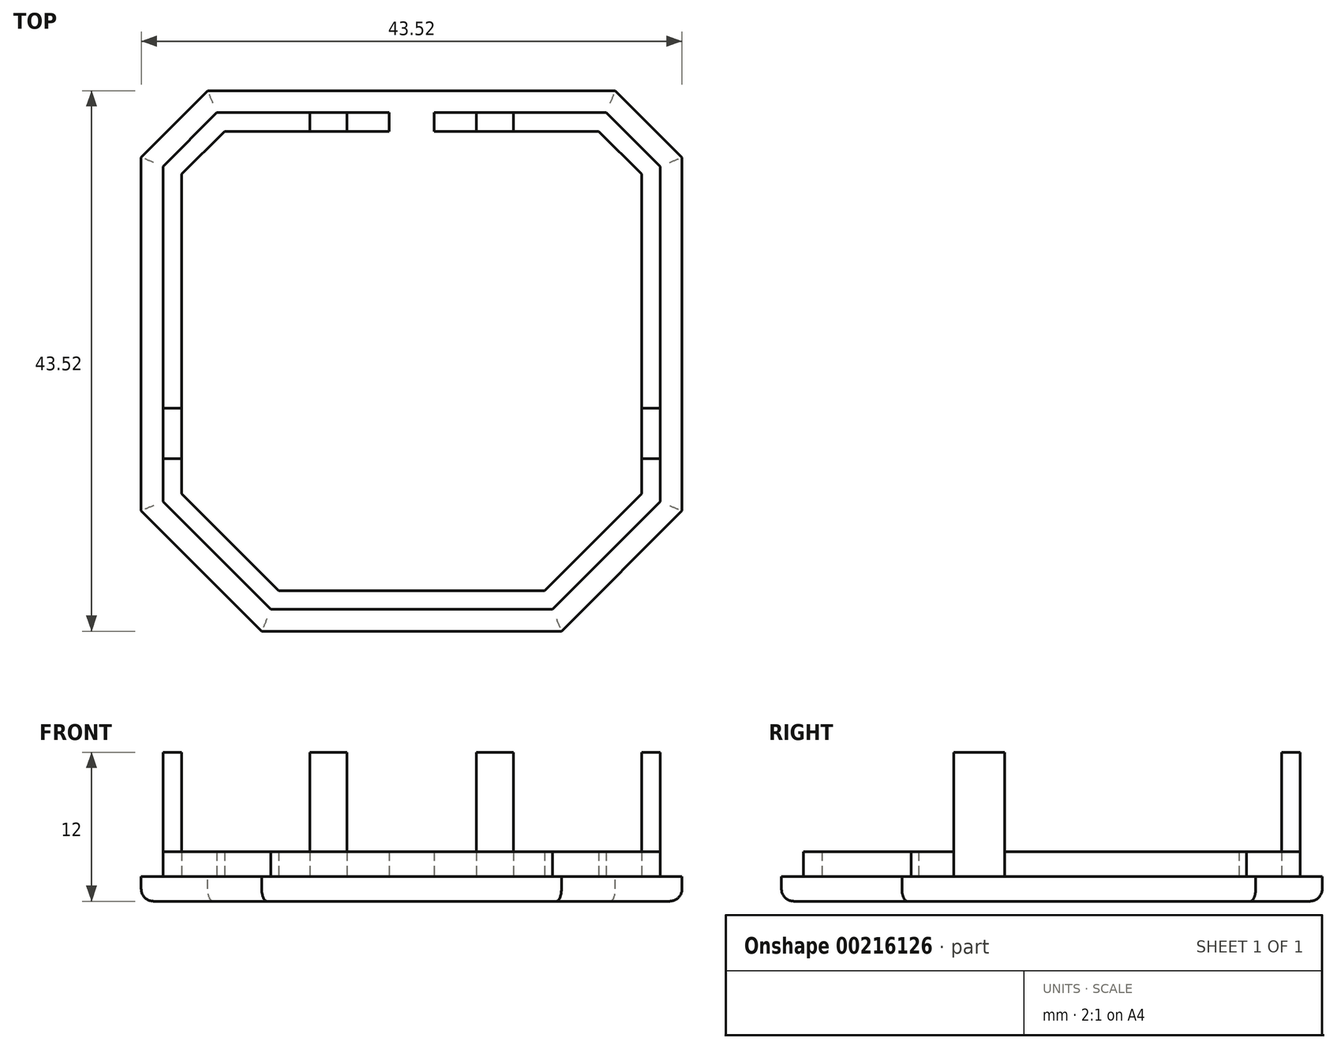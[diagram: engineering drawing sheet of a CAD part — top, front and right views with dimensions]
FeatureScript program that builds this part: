
annotation { "Feature Type Name" : "Feature", "Feature Type Description" : "" }
export const myFeature = defineFeature(function(context is Context, id is Id, definition is map)
    precondition{}
    {
        {
            var Q0;
            Q0=qCreatedBy(makeId("Top.planeOp"),FACE);
            var sketch = newSketch(context, id + "F0", { "sketchPlane" : qUnion([Q0])});
            skLineSegment(sketch, "E0", {"start": v(-56.85, 1.5) * mm, "end": v(-30.15, 1.5) * mm, "construction": true});
            skLineSegment(sketch, "E1", {"start": v(-0.95, 49.22) * mm, "end": v(-0.95, -52.62) * mm, "construction": true});
            skPoint(sketch, "E2", {"position": v(28.25, 1.5) * mm});
            skLineSegment(sketch, "E3.trimOffspring", {"start": v(-27.15, 1.5) * mm, "end": v(25.25, 1.5) * mm, "construction": true});
            skLineSegment(sketch, "E4.trimOffspring", {"start": v(28.25, 1.5) * mm, "end": v(65.36, 1.5) * mm, "construction": true});
            skLineSegment(sketch, "E5.bottom", {"start": v(10.38, -21.7) * mm, "end": v(-12.28, -21.7) * mm});
            skLineSegment(sketch, "E5.top", {"start": v(14.72, 18.3) * mm, "end": v(-16.62, 18.3) * mm});
            skLineSegment(sketch, "E5.left", {"start": v(19.05, -13.03) * mm, "end": v(19.05, 13.97) * mm});
            skLineSegment(sketch, "E5.right", {"start": v(-20.95, -13.03) * mm, "end": v(-20.95, 13.97) * mm});
            skPoint(sketch, "E5.middle", {"position": v(-0.95, -1.7) * mm});
            skPoint(sketch, "E6.visualSharp", {"position": v(-20.95, 18.3) * mm});
            skPoint(sketch, "E7.visualSharp", {"position": v(19.05, 18.3) * mm});
            skPoint(sketch, "E8.visualSharp", {"position": v(19.05, -21.7) * mm});
            skPoint(sketch, "E9.visualSharp", {"position": v(-20.95, -21.7) * mm});
            skLineSegment(sketch, "E10", {"start": v(-20.95, 13.97) * mm, "end": v(-16.62, 18.3) * mm});
            skLineSegment(sketch, "E11", {"start": v(14.72, 18.3) * mm, "end": v(19.05, 13.97) * mm});
            skLineSegment(sketch, "E12", {"start": v(19.05, -13.03) * mm, "end": v(10.38, -21.7) * mm});
            skLineSegment(sketch, "E13", {"start": v(-20.95, -13.03) * mm, "end": v(-12.28, -21.7) * mm});
            skLineSegment(sketch, "E14.0", {"start": v(-22.71, -13.76) * mm, "end": v(-13.01, -23.46) * mm});
            skLineSegment(sketch, "E14.1", {"start": v(11.1, -23.46) * mm, "end": v(-13.01, -23.46) * mm});
            skLineSegment(sketch, "E14.2", {"start": v(-22.71, -13.76) * mm, "end": v(-22.71, 14.7) * mm});
            skLineSegment(sketch, "E14.3", {"start": v(20.81, -13.76) * mm, "end": v(11.1, -23.46) * mm});
            skLineSegment(sketch, "E14.4", {"start": v(-22.71, 14.7) * mm, "end": v(-17.35, 20.06) * mm});
            skLineSegment(sketch, "E14.5", {"start": v(15.45, 20.06) * mm, "end": v(-17.35, 20.06) * mm});
            skLineSegment(sketch, "E14.6", {"start": v(15.45, 20.06) * mm, "end": v(20.81, 14.7) * mm});
            skLineSegment(sketch, "E14.7", {"start": v(20.81, -13.76) * mm, "end": v(20.81, 14.7) * mm});
            skPoint(sketch, "E15.orphan", {"position": v(32.35, 7.83) * mm});
            skPoint(sketch, "E16.orphan", {"position": v(32.35, -4.83) * mm});
            skPoint(sketch, "E17.orphan", {"position": v(-30.54, -4.83) * mm});
            skPoint(sketch, "E18.orphan", {"position": v(-30.54, 7.83) * mm});
            skPoint(sketch, "E19.center.orphan", {"position": v(-9.84, 17.42) * mm});
            skPoint(sketch, "E20.center.orphan", {"position": v(-9.84, -20.93) * mm});
            skLineSegment(sketch, "E21.0", {"start": v(14.1, 16.8) * mm, "end": v(17.55, 13.35) * mm});
            skLineSegment(sketch, "E21.1", {"start": v(17.55, -12.4) * mm, "end": v(17.55, 13.35) * mm});
            skLineSegment(sketch, "E21.2", {"start": v(14.1, 16.8) * mm, "end": v(-16, 16.8) * mm});
            skLineSegment(sketch, "E21.3", {"start": v(17.55, -12.4) * mm, "end": v(9.76, -20.2) * mm});
            skLineSegment(sketch, "E21.4", {"start": v(-19.45, 13.35) * mm, "end": v(-16, 16.8) * mm});
            skLineSegment(sketch, "E21.5", {"start": v(-19.45, -12.4) * mm, "end": v(-19.45, 13.35) * mm});
            skLineSegment(sketch, "E21.6", {"start": v(-19.45, -12.4) * mm, "end": v(-11.66, -20.2) * mm});
            skLineSegment(sketch, "E21.7", {"start": v(9.76, -20.2) * mm, "end": v(-11.66, -20.2) * mm});
            skLineSegment(sketch, "E22", {"start": v(-20.95, -9.58) * mm, "end": v(-19.45, -9.58) * mm});
            skLineSegment(sketch, "E23", {"start": v(-19.45, -9.58) * mm, "end": v(-19.45, -5.5) * mm});
            skLineSegment(sketch, "E24", {"start": v(-19.45, -5.5) * mm, "end": v(-20.95, -5.5) * mm});
            skLineSegment(sketch, "E25.MirrorCS", {"start": v(19.05, -9.58) * mm, "end": v(17.55, -9.58) * mm});
            skLineSegment(sketch, "E26.MirrorCS", {"start": v(17.55, -5.5) * mm, "end": v(19.05, -5.5) * mm});
            skLineSegment(sketch, "E27", {"start": v(-9.15, 18.3) * mm, "end": v(-9.15, 16.8) * mm});
            skLineSegment(sketch, "E28", {"start": v(-9.15, 16.8) * mm, "end": v(-6.15, 16.8) * mm});
            skLineSegment(sketch, "E29", {"start": v(-6.15, 16.8) * mm, "end": v(-6.15, 18.3) * mm});
            skPoint(sketch, "E30.end.orphan", {"position": v(-2.77, 18.3) * mm});
            skPoint(sketch, "E30.start.orphan", {"position": v(-2.77, 16.8) * mm});
            skPoint(sketch, "E31.MirrorCS.end.orphan", {"position": v(0.86, 18.3) * mm});
            skPoint(sketch, "E31.MirrorCS.start.orphan", {"position": v(0.86, 16.8) * mm});
            skLineSegment(sketch, "E32.MirrorCS", {"start": v(7.25, 18.3) * mm, "end": v(7.25, 16.8) * mm});
            skLineSegment(sketch, "E33.MirrorCS", {"start": v(4.25, 16.8) * mm, "end": v(4.25, 18.3) * mm});
            skLineSegment(sketch, "E34.MirrorCS", {"start": v(7.25, 16.8) * mm, "end": v(4.25, 16.8) * mm});
            skLineSegment(sketch, "E35", {"start": v(-2.77, 18.3) * mm, "end": v(-2.77, 16.8) * mm});
            skLineSegment(sketch, "E36", {"start": v(0.86, 18.3) * mm, "end": v(0.86, 16.8) * mm});
            skSolve(sketch);
        }
        {
            var Q0;
            Q0 = qSketchRegion(id + "F0", true);
            var Q1;
            Q1=makeQuery(id+"F0.imprint","IMPRINT",FACE,{"disambiguationData":[TD([[makeQuery(id+"F0.imprint","IMPRINT",EDGE,{"derivedFrom":sQuery(id+"F0.wireOp",EDGE,"E5.left")}),1.0]])]});
            var Q2;
            {var subQ0=sQuery(id+"F0.wireOp",EDGE,"E19");Q2=makeQuery(id+"F0.imprint","IMPRINT",FACE,{"disambiguationData":[TD([[makeQuery(id+"F0.imprint","IMPRINT",EDGE,{"derivedFrom":subQ0}),1.0]])]});}
            var Q3;
            {var subQ0=sQuery(id+"F0.wireOp",EDGE,"4e1065f4-3c0d-4255-a0ed-20f52c7de798.MirrorC");Q3=makeQuery(id+"F0.imprint","IMPRINT",FACE,{"disambiguationData":[TD([[makeQuery(id+"F0.imprint","IMPRINT",EDGE,{"derivedFrom":subQ0}),-1.0]])]});}
            var Q4;
            {var subQ0=sQuery(id+"F0.wireOp",EDGE,"f484cf5a-7d54-4800-a930-bd30d667224f.MirrorC");Q4=makeQuery(id+"F0.imprint","IMPRINT",FACE,{"disambiguationData":[TD([[makeQuery(id+"F0.imprint","IMPRINT",EDGE,{"derivedFrom":subQ0}),-1.0]])]});}
            var Q5;
            {var subQ0=sQuery(id+"F0.wireOp",EDGE,"E20");Q5=makeQuery(id+"F0.imprint","IMPRINT",FACE,{"disambiguationData":[TD([[makeQuery(id+"F0.imprint","IMPRINT",EDGE,{"derivedFrom":subQ0}),1.0]])]});}
            var Q6;
            Q6=makeQuery(id+"F0.imprint","IMPRINT",FACE,{"disambiguationData":[TD([[makeQuery(id+"F0.imprint","IMPRINT",EDGE,{"derivedFrom":sQuery(id+"F0.wireOp",EDGE,"E21.0")}),-1.0]])]});
            var Q7;
            {var subQ1=sQuery(id+"F0.wireOp",EDGE,"E11");Q7=makeQuery(id+"F0.imprint","IMPRINT",FACE,{"disambiguationData":[TD([[makeQuery(id+"F0.imprint","IMPRINT",EDGE,{"derivedFrom":subQ1}),-1.0]])]});}
            var Q8;
            {var subQ0=sQuery(id+"F0.wireOp",EDGE,"E10");Q8=makeQuery(id+"F0.imprint","IMPRINT",FACE,{"disambiguationData":[TD([[makeQuery(id+"F0.imprint","IMPRINT",EDGE,{"derivedFrom":subQ0}),-1.0]])]});}
            var Q9;
            Q9=makeQuery(id+"F0.imprint","IMPRINT",FACE,{"disambiguationData":[TD([[makeQuery(id+"F0.imprint","IMPRINT",EDGE,{"derivedFrom":sQuery(id+"F0.wireOp",EDGE,"E5.bottom")}),-1.0]])]});
            var Q10;
            {var subQ0=sQuery(id+"F0.wireOp",EDGE,"E30");Q10=makeQuery(id+"F0.imprint","IMPRINT",FACE,{"disambiguationData":[TD([[makeQuery(id+"F0.imprint","IMPRINT",EDGE,{"derivedFrom":subQ0}),-1.0]])]});}
            var Q11;
            {var subQ0=sQuery(id+"F0.wireOp",EDGE,"E22");Q11=makeQuery(id+"F0.imprint","IMPRINT",FACE,{"disambiguationData":[TD([[makeQuery(id+"F0.imprint","IMPRINT",EDGE,{"derivedFrom":subQ0}),1.0]])]});}
            var Q12;
            {var subQ0=sQuery(id+"F0.wireOp",EDGE,"E32.MirrorCS");Q12=makeQuery(id+"F0.imprint","IMPRINT",FACE,{"disambiguationData":[TD([[makeQuery(id+"F0.imprint","IMPRINT",EDGE,{"derivedFrom":subQ0}),-1.0]])]});}
            var Q13;
            {var subQ0=sQuery(id+"F0.wireOp",EDGE,"E29");Q13=makeQuery(id+"F0.imprint","IMPRINT",FACE,{"disambiguationData":[TD([[makeQuery(id+"F0.imprint","IMPRINT",EDGE,{"derivedFrom":subQ0}),-1.0]])]});}
            var Q14;
            {var subQ0=sQuery(id+"F0.wireOp",EDGE,"E27");Q14=makeQuery(id+"F0.imprint","IMPRINT",FACE,{"disambiguationData":[TD([[makeQuery(id+"F0.imprint","IMPRINT",EDGE,{"derivedFrom":subQ0}),1.0]])]});}
            var Q15;
            {var subQ0=sQuery(id+"F0.wireOp",EDGE,"E33.MirrorCS");Q15=makeQuery(id+"F0.imprint","IMPRINT",FACE,{"disambiguationData":[TD([[makeQuery(id+"F0.imprint","IMPRINT",EDGE,{"derivedFrom":subQ0}),1.0]])]});}
            var Q16;
            {var subQ0=sQuery(id+"F0.wireOp",EDGE,"E35");Q16=makeQuery(id+"F0.imprint","IMPRINT",FACE,{"disambiguationData":[TD([[makeQuery(id+"F0.imprint","IMPRINT",EDGE,{"derivedFrom":subQ0}),1.0]])]});}
            extrude(context, id + "F1", {"entities" : qUnion([Q0, Q1, Q2, Q3, Q4, Q5, Q6, Q7, Q8, Q9, Q10, Q11, Q12, Q13, Q14, Q15, Q16]), "oppositeDirection" : true, "depth" : 2 * mm});
        }
        {
            var Q0;
            Q0=makeQuery(id+"F0.imprint","IMPRINT",FACE,{"disambiguationData":[TD([[makeQuery(id+"F0.imprint","IMPRINT",EDGE,{"derivedFrom":sQuery(id+"F0.wireOp",EDGE,"E5.bottom")}),-1.0]])]});
            var Q1;
            {var subQ0=sQuery(id+"F0.wireOp",EDGE,"E10");Q1=makeQuery(id+"F0.imprint","IMPRINT",FACE,{"disambiguationData":[TD([[makeQuery(id+"F0.imprint","IMPRINT",EDGE,{"derivedFrom":subQ0}),-1.0]])]});}
            var Q2;
            {var subQ1=sQuery(id+"F0.wireOp",EDGE,"E11");Q2=makeQuery(id+"F0.imprint","IMPRINT",FACE,{"disambiguationData":[TD([[makeQuery(id+"F0.imprint","IMPRINT",EDGE,{"derivedFrom":subQ1}),-1.0]])]});}
            var Q3;
            {var subQ0=sQuery(id+"F0.wireOp",EDGE,"E29");Q3=makeQuery(id+"F0.imprint","IMPRINT",FACE,{"disambiguationData":[TD([[makeQuery(id+"F0.imprint","IMPRINT",EDGE,{"derivedFrom":subQ0}),-1.0]])]});}
            var Q4;
            {var subQ0=sQuery(id+"F0.wireOp",EDGE,"E33.MirrorCS");Q4=makeQuery(id+"F0.imprint","IMPRINT",FACE,{"disambiguationData":[TD([[makeQuery(id+"F0.imprint","IMPRINT",EDGE,{"derivedFrom":subQ0}),1.0]])]});}
            extrude(context, id + "F2", {"entities" : qUnion([Q0, Q1, Q2, Q3, Q4]), "operationType" : NewBodyOperationType.ADD, "depth" : 2 * mm});
        }
        {
            var Q0;
            {var subQ0=sQuery(id+"F0.wireOp",EDGE,"E22");Q0=makeQuery(id+"F0.imprint","IMPRINT",FACE,{"disambiguationData":[TD([[makeQuery(id+"F0.imprint","IMPRINT",EDGE,{"derivedFrom":subQ0}),1.0]])]});}
            var Q1;
            {var subQ0=sQuery(id+"F0.wireOp",EDGE,"E25.MirrorCS");Q1=makeQuery(id+"F0.imprint","IMPRINT",FACE,{"disambiguationData":[TD([[makeQuery(id+"F0.imprint","IMPRINT",EDGE,{"derivedFrom":subQ0}),-1.0]])]});}
            var Q2;
            {var subQ0=sQuery(id+"F0.wireOp",EDGE,"E30");Q2=makeQuery(id+"F0.imprint","IMPRINT",FACE,{"disambiguationData":[TD([[makeQuery(id+"F0.imprint","IMPRINT",EDGE,{"derivedFrom":subQ0}),-1.0]])]});}
            var Q3;
            {var subQ0=sQuery(id+"F0.wireOp",EDGE,"E27");Q3=makeQuery(id+"F0.imprint","IMPRINT",FACE,{"disambiguationData":[TD([[makeQuery(id+"F0.imprint","IMPRINT",EDGE,{"derivedFrom":subQ0}),1.0]])]});}
            var Q4;
            {var subQ0=sQuery(id+"F0.wireOp",EDGE,"E32.MirrorCS");Q4=makeQuery(id+"F0.imprint","IMPRINT",FACE,{"disambiguationData":[TD([[makeQuery(id+"F0.imprint","IMPRINT",EDGE,{"derivedFrom":subQ0}),-1.0]])]});}
            extrude(context, id + "F3", {"entities" : qUnion([Q0, Q1, Q2, Q3, Q4]), "depth" : 10 * mm});
        }
        {
            var Q0;
            Q0=makeQuery(id+"F1.opExtrude","CAP_FACE",FACE,{"disambiguationData":[OSD([sQuery(id+"F0.wireOp",EDGE,"E14.0"),sQuery(id+"F0.wireOp",EDGE,"E14.1"),sQuery(id+"F0.wireOp",EDGE,"E14.2"),sQuery(id+"F0.wireOp",EDGE,"E14.3"),sQuery(id+"F0.wireOp",EDGE,"E14.4"),sQuery(id+"F0.wireOp",EDGE,"E14.5"),sQuery(id+"F0.wireOp",EDGE,"E14.6"),sQuery(id+"F0.wireOp",EDGE,"E14.7")])],"isStart":false});
            fillet(context, id + "F4", {"entities" : qUnion([Q0]), "radius" : 1 * mm, "tangentPropagation" : true, "allowEdgeOverflow" : false});
        }
    });
